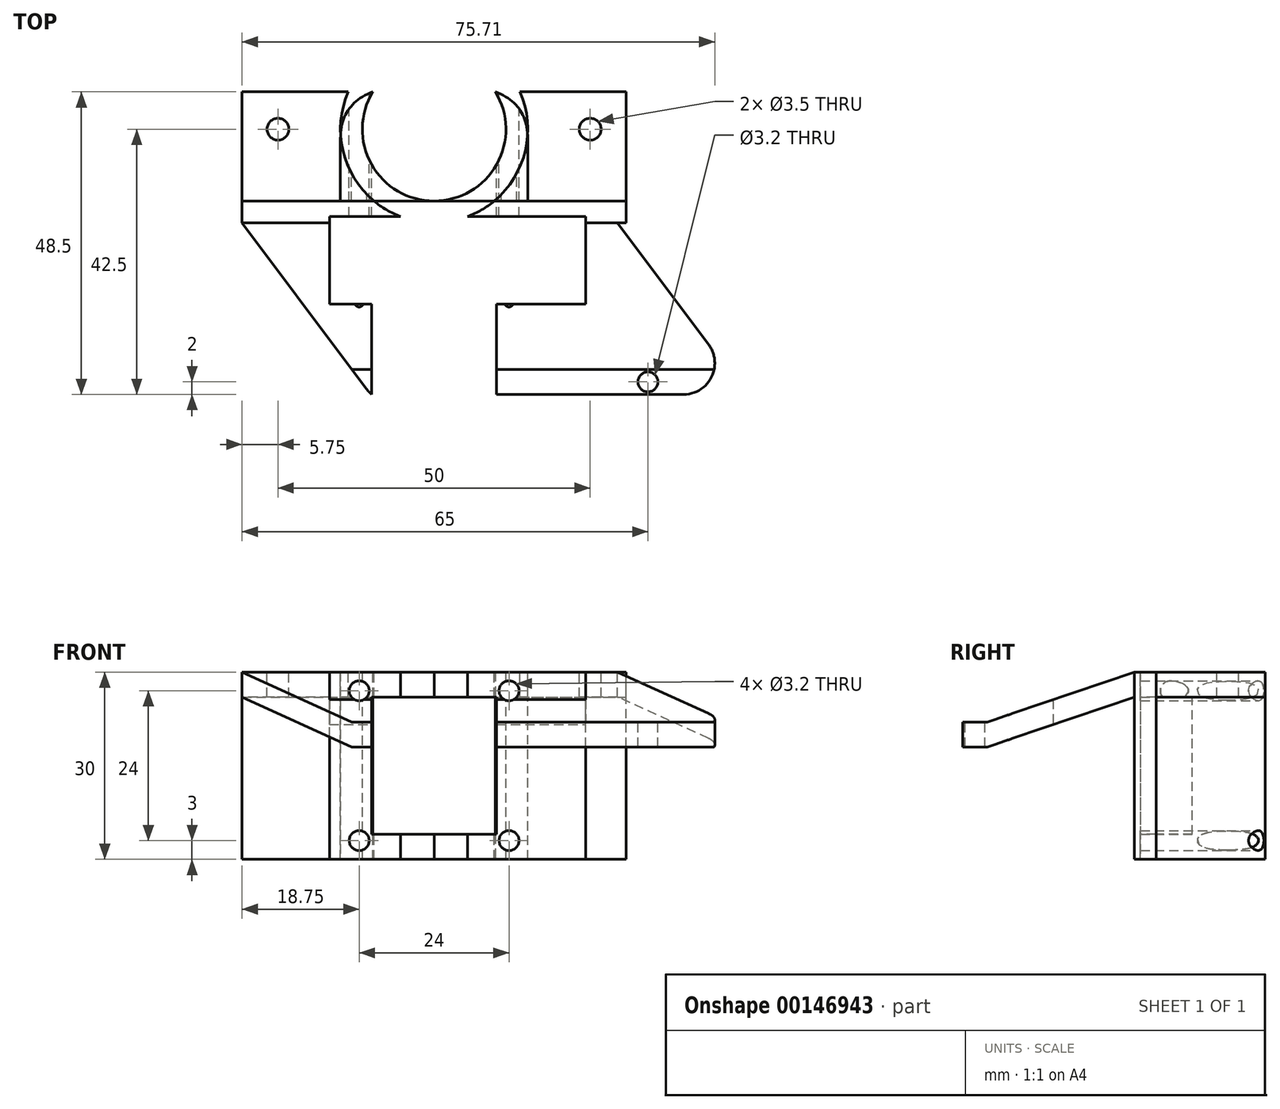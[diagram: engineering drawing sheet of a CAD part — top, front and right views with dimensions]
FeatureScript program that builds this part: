
annotation { "Feature Type Name" : "Feature", "Feature Type Description" : "" }
export const myFeature = defineFeature(function(context is Context, id is Id, definition is map)
    precondition{}
    {
        {
            var Q0;
            Q0=qCreatedBy(makeId("Top.planeOp"),FACE);
            var sketch = newSketch(context, id + "F0", { "sketchPlane" : qUnion([Q0])});
            skLineSegment(sketch, "E0", {"start": v(-25, 0) * mm, "end": v(25, 0) * mm, "construction": true});
            skCircle(sketch, "E1", {"center": v(0, 0) * mm, "radius": 15 * mm, "construction": true});
            skCircle(sketch, "E2", {"center": v(-25, 0) * mm, "radius": 1.75 * mm});
            skCircle(sketch, "E3", {"center": v(25, 0) * mm, "radius": 1.75 * mm});
            skLineSegment(sketch, "E4", {"start": v(-26.75, 0) * mm, "end": v(-30.75, 0) * mm, "construction": true});
            skLineSegment(sketch, "E5", {"start": v(26.75, 0) * mm, "end": v(30.75, 0) * mm, "construction": true});
            skLineSegment(sketch, "E6.bottom", {"start": v(-30.75, 6) * mm, "end": v(30.75, 6) * mm});
            skLineSegment(sketch, "E6.top", {"start": v(-30.75, -15) * mm, "end": v(30.75, -15) * mm});
            skLineSegment(sketch, "E6.left", {"start": v(-30.75, 6) * mm, "end": v(-30.75, -15) * mm});
            skLineSegment(sketch, "E6.right", {"start": v(30.75, 6) * mm, "end": v(30.75, -15) * mm});
            skArc(sketch, "E7", {"start": v(13.75, 6) * mm, "mid": v(0, -15) * mm, "end": v(-13.75, 6) * mm});
            skLineSegment(sketch, "E8.top", {"start": v(-30.75, -11.5) * mm, "end": v(30.75, -11.5) * mm});
            skLineSegment(sketch, "E8.left", {"start": v(-30.75, -15) * mm, "end": v(-30.75, -11.5) * mm});
            skLineSegment(sketch, "E8.right", {"start": v(30.75, -15) * mm, "end": v(30.75, -11.5) * mm});
            skCircle(sketch, "E9", {"center": v(0, 0) * mm, "radius": 11.5 * mm});
            skLineSegment(sketch, "E10", {"start": v(15, -11.5) * mm, "end": v(15, 0) * mm});
            skLineSegment(sketch, "E11", {"start": v(-15, 0) * mm, "end": v(-15, -11.5) * mm});
            skSolve(sketch);
        }
        {
            var Q0;
            Q0=makeQuery(id+"F0.imprint","IMPRINT",FACE,{"disambiguationData":[TD([[makeQuery(id+"F0.imprint","IMPRINT",EDGE,{"derivedFrom":sQuery(id+"F0.wireOp",EDGE,"E2")}),-1.0]])]});
            var Q1;
            {var subQ0=sQuery(id+"F0.wireOp",EDGE,"E11");Q1=makeQuery(id+"F0.imprint","IMPRINT",FACE,{"disambiguationData":[TD([[makeQuery(id+"F0.imprint","IMPRINT",EDGE,{"derivedFrom":subQ0}),1.0]])]});}
            var Q2;
            {var subQ0=sQuery(id+"F0.wireOp",EDGE,"E10");Q2=makeQuery(id+"F0.imprint","IMPRINT",FACE,{"disambiguationData":[TD([[makeQuery(id+"F0.imprint","IMPRINT",EDGE,{"derivedFrom":subQ0}),1.0]])]});}
            var Q3;
            Q3=makeQuery(id+"F0.imprint","IMPRINT",FACE,{"disambiguationData":[TD([[makeQuery(id+"F0.imprint","IMPRINT",EDGE,{"derivedFrom":sQuery(id+"F0.wireOp",EDGE,"E3")}),-1.0]])]});
            extrude(context, id + "F1", {"entities" : qUnion([Q0, Q1, Q2, Q3]), "oppositeDirection" : true, "depth" : 4 * mm, "offsetDistance" : 25 * mm});
        }
        {
            var Q0;
            Q0=makeQuery(id+"F0.imprint","IMPRINT",FACE,{"disambiguationData":[TD([[makeQuery(id+"F0.imprint","IMPRINT",EDGE,{"derivedFrom":sQuery(id+"F0.wireOp",EDGE,"E6.top")}),1.0]])]});
            var Q1;
            {var subQ0=sQuery(id+"F0.wireOp",EDGE,"E7");var subQ3=sQuery(id+"F0.wireOp",EDGE,"E6.bottom");var subQ4=makeQuery(id+"F0.imprint","INTERSECT",VERTEX,{"disambiguationData":[OD(1.0)],"derivedFrom":[subQ3,subQ0]});Q1=makeQuery(id+"F0.imprint","IMPRINT",FACE,{"disambiguationData":[TD([[makeQuery(id+"F0.imprint","IMPRINT",EDGE,{"disambiguationData":[TD([[subQ4,-1.0]])],"derivedFrom":subQ3}),-1.0]])]});}
            var Q2;
            {var subQ0=sQuery(id+"F0.wireOp",EDGE,"E11");Q2=makeQuery(id+"F0.imprint","IMPRINT",FACE,{"disambiguationData":[TD([[makeQuery(id+"F0.imprint","IMPRINT",EDGE,{"derivedFrom":subQ0}),1.0]])]});}
            var Q3;
            {var subQ0=sQuery(id+"F0.wireOp",EDGE,"E10");Q3=makeQuery(id+"F0.imprint","IMPRINT",FACE,{"disambiguationData":[TD([[makeQuery(id+"F0.imprint","IMPRINT",EDGE,{"derivedFrom":subQ0}),1.0]])]});}
            var Q4;
            {var subQ0=sQuery(id+"F0.wireOp",EDGE,"E7");var subQ4=sQuery(id+"F0.wireOp",EDGE,"E6.bottom");var subQ5=makeQuery(id+"F0.imprint","INTERSECT",VERTEX,{"disambiguationData":[OD(0.0)],"derivedFrom":[subQ4,subQ0]});Q4=makeQuery(id+"F0.imprint","IMPRINT",FACE,{"disambiguationData":[TD([[makeQuery(id+"F0.imprint","IMPRINT",EDGE,{"disambiguationData":[TD([[subQ5,1.0]])],"derivedFrom":subQ4}),-1.0]])]});}
            var Q5;
            {var subQ0=sQuery(id+"F0.wireOp",EDGE,"E7");var subQ1=makeQuery(id+"F0.imprint","INTERSECT",VERTEX,{"derivedFrom":[subQ0,sQuery(id+"F0.wireOp",EDGE,"E6.top")]});Q5=makeQuery(id+"F0.imprint","IMPRINT",FACE,{"disambiguationData":[TD([[makeQuery(id+"F0.imprint","IMPRINT",EDGE,{"disambiguationData":[TD([[subQ1,1.0]])],"derivedFrom":subQ0}),-1.0]])]});}
            extrude(context, id + "F2", {"entities" : qUnion([Q0, Q1, Q2, Q3, Q4, Q5]), "oppositeDirection" : true, "depth" : 30 * mm, "offsetDistance" : 25 * mm});
        }
        {
            var Q0;
            {var subQ0=sQuery(id+"F0.wireOp",EDGE,"E7");var subQ1=sQuery(id+"F0.wireOp",EDGE,"E6.bottom");Q0=makeQuery(id+"F2.opExtrude","SWEPT_EDGE",EDGE,{"disambiguationData":[OSD([subQ1,subQ0]),TDD([makeQuery(id+"F0.imprint","INTERSECT",VERTEX,{"disambiguationData":[OD(1.0)],"derivedFrom":[subQ1,subQ0]})])]});}
            var Q1;
            {var subQ0=sQuery(id+"F0.wireOp",EDGE,"E7");var subQ1=sQuery(id+"F0.wireOp",EDGE,"E6.bottom");Q1=makeQuery(id+"F2.opExtrude","SWEPT_EDGE",EDGE,{"disambiguationData":[OSD([subQ1,subQ0]),TDD([makeQuery(id+"F0.imprint","INTERSECT",VERTEX,{"disambiguationData":[OD(0.0)],"derivedFrom":[subQ1,subQ0]})])]});}
            fillet(context, id + "F3", {"entities" : qUnion([Q0, Q1]), "radius" : 8 * mm, "tangentPropagation" : true, "rho" : 0.5, "crossSection" : FilletCrossSection.CONIC, "allowEdgeOverflow" : false});
        }
        {
            var Q0;
            Q0=qCreatedBy(makeId("Front.planeOp"),FACE);
            var sketch = newSketch(context, id + "F4", { "sketchPlane" : qUnion([Q0])});
            skLineSegment(sketch, "E12", {"start": v(0, 0) * mm, "end": v(0, -30) * mm, "construction": true});
            skLineSegment(sketch, "E13.bottom", {"start": v(10, -4) * mm, "end": v(-10, -4) * mm});
            skLineSegment(sketch, "E13.top", {"start": v(10, -26) * mm, "end": v(-10, -26) * mm});
            skLineSegment(sketch, "E13.left", {"start": v(10, -4) * mm, "end": v(10, -26) * mm});
            skLineSegment(sketch, "E13.right", {"start": v(-10, -4) * mm, "end": v(-10, -26) * mm});
            skPoint(sketch, "E13.middle", {"position": v(0, -15) * mm});
            skLineSegment(sketch, "E14.bottom", {"start": v(12, -3) * mm, "end": v(-12, -3) * mm, "construction": true});
            skLineSegment(sketch, "E14.top", {"start": v(12, -27) * mm, "end": v(-12, -27) * mm, "construction": true});
            skLineSegment(sketch, "E14.left", {"start": v(12, -3) * mm, "end": v(12, -27) * mm, "construction": true});
            skLineSegment(sketch, "E14.right", {"start": v(-12, -3) * mm, "end": v(-12, -27) * mm, "construction": true});
            skCircle(sketch, "E15", {"center": v(12, -3) * mm, "radius": 1.6 * mm});
            skCircle(sketch, "E16", {"center": v(-12, -3) * mm, "radius": 1.6 * mm});
            skCircle(sketch, "E17", {"center": v(-12, -27) * mm, "radius": 1.6 * mm});
            skCircle(sketch, "E18", {"center": v(12, -27) * mm, "radius": 1.6 * mm});
            skSolve(sketch);
        }
        {
            var Q0;
            Q0=qCreatedBy(makeId("Right.planeOp"),FACE);
            var sketch = newSketch(context, id + "F5", { "sketchPlane" : qUnion([Q0])});
            skLineSegment(sketch, "E19", {"start": v(-40.5, 0) * mm, "end": v(0, 0) * mm, "construction": true});
            skLineSegment(sketch, "E20", {"start": v(-40.5, 0) * mm, "end": v(-40.5, -12) * mm, "construction": true});
            skLineSegment(sketch, "E21", {"start": v(-42.5, -12) * mm, "end": v(-38.5, -12) * mm});
            skLineSegment(sketch, "E22", {"start": v(-42.5, -12) * mm, "end": v(-42.5, -8) * mm});
            skLineSegment(sketch, "E23", {"start": v(-42.5, -8) * mm, "end": v(-38.5, -8) * mm});
            skLineSegment(sketch, "E24", {"start": v(-38.5, -8) * mm, "end": v(-38.5, -12) * mm});
            skLineSegment(sketch, "E25", {"start": v(-38.5, -8) * mm, "end": v(-15, 0) * mm});
            skLineSegment(sketch, "E26", {"start": v(-15, 0) * mm, "end": v(-15, -4) * mm});
            skLineSegment(sketch, "E27", {"start": v(-15, -4) * mm, "end": v(-15, 0) * mm});
            skLineSegment(sketch, "E28", {"start": v(-38.5, -12) * mm, "end": v(-15, -4) * mm});
            skSolve(sketch);
        }
        {
            var Q0;
            Q0=makeQuery(id+"F5.imprint","IMPRINT",FACE,{"disambiguationData":[TD([[makeQuery(id+"F5.imprint","IMPRINT",EDGE,{"derivedFrom":sQuery(id+"F5.wireOp",EDGE,"E21")}),1.0]])]});
            var Q1;
            Q1=makeQuery(id+"F5.imprint","IMPRINT",FACE,{"disambiguationData":[TD([[makeQuery(id+"F5.imprint","IMPRINT",EDGE,{"derivedFrom":sQuery(id+"F5.wireOp",EDGE,"E24")}),1.0]])]});
            extrude(context, id + "F6", {"entities" : qUnion([Q0, Q1]), "endBound" : BoundingType.SYMMETRIC, "depth" : 100 * mm});
        }
        {
            var Q0;
            Q0=makeQuery(id+"F4.imprint","IMPRINT",FACE,{"disambiguationData":[TD([[makeQuery(id+"F4.imprint","IMPRINT",EDGE,{"derivedFrom":sQuery(id+"F4.wireOp",EDGE,"E13.bottom")}),1.0]])]});
            extrude(context, id + "F7", {"entities" : qUnion([Q0]), "operationType" : NewBodyOperationType.REMOVE, "depth" : 111 * mm});
        }
        {
            var Q0;
            Q0=makeQuery(id+"F4.imprint","IMPRINT",FACE,{"disambiguationData":[TD([[makeQuery(id+"F4.imprint","IMPRINT",EDGE,{"derivedFrom":sQuery(id+"F4.wireOp",EDGE,"E15")}),1.0]])]});
            var Q1;
            Q1=makeQuery(id+"F4.imprint","IMPRINT",FACE,{"disambiguationData":[TD([[makeQuery(id+"F4.imprint","IMPRINT",EDGE,{"derivedFrom":sQuery(id+"F4.wireOp",EDGE,"E16")}),1.0]])]});
            var Q2;
            Q2=makeQuery(id+"F4.imprint","IMPRINT",FACE,{"disambiguationData":[TD([[makeQuery(id+"F4.imprint","IMPRINT",EDGE,{"derivedFrom":sQuery(id+"F4.wireOp",EDGE,"E17")}),1.0]])]});
            var Q3;
            Q3=makeQuery(id+"F4.imprint","IMPRINT",FACE,{"disambiguationData":[TD([[makeQuery(id+"F4.imprint","IMPRINT",EDGE,{"derivedFrom":sQuery(id+"F4.wireOp",EDGE,"E18")}),1.0]])]});
            extrude(context, id + "F8", {"entities" : qUnion([Q0, Q1, Q2, Q3]), "operationType" : NewBodyOperationType.REMOVE, "endBound" : BoundingType.SYMMETRIC, "depth" : 100 * mm});
        }
        {
            var Q0;
            Q0=qCreatedBy(makeId("Top.planeOp"),FACE);
            var sketch = newSketch(context, id + "F9", { "sketchPlane" : qUnion([Q0])});
            skLineSegment(sketch, "E29", {"start": v(-30.75, -40.5) * mm, "end": v(-5.75, -40.5) * mm, "construction": true});
            skLineSegment(sketch, "E30", {"start": v(-5.75, -40.5) * mm, "end": v(34.25, -40.5) * mm, "construction": true});
            skLineSegment(sketch, "E31", {"start": v(-30.75, -15) * mm, "end": v(-30.75, -38.5) * mm, "construction": true});
            skCircle(sketch, "E32", {"center": v(-5.75, -40.5) * mm, "radius": 1.6 * mm});
            skCircle(sketch, "E33", {"center": v(34.25, -40.5) * mm, "radius": 1.6 * mm});
            skLineSegment(sketch, "E34", {"start": v(-30.75, -15) * mm, "end": v(-10.16, -42.52) * mm});
            skLineSegment(sketch, "E35", {"start": v(49.96, -42.52) * mm, "end": v(29.37, -15) * mm});
            skLineSegment(sketch, "E36", {"start": v(29.37, -15) * mm, "end": v(-30.75, -15) * mm});
            skLineSegment(sketch, "E37", {"start": v(-30.75, -15) * mm, "end": v(-55.36, -15) * mm});
            skLineSegment(sketch, "E38", {"start": v(-55.36, -15) * mm, "end": v(-55.36, -47.4) * mm});
            skLineSegment(sketch, "E39", {"start": v(-55.36, -47.4) * mm, "end": v(60.75, -47.4) * mm});
            skLineSegment(sketch, "E40", {"start": v(60.75, -47.4) * mm, "end": v(60.75, -15) * mm});
            skLineSegment(sketch, "E41", {"start": v(60.75, -15) * mm, "end": v(29.37, -15) * mm});
            skLineSegment(sketch, "E42", {"start": v(49.96, -42.52) * mm, "end": v(-10.16, -42.52) * mm});
            skSolve(sketch);
        }
        {
            var Q0;
            Q0=makeQuery(id+"F9.imprint","IMPRINT",FACE,{"disambiguationData":[TD([[makeQuery(id+"F9.imprint","IMPRINT",EDGE,{"derivedFrom":sQuery(id+"F9.wireOp",EDGE,"E32")}),1.0]])]});
            var Q1;
            Q1=makeQuery(id+"F9.imprint","IMPRINT",FACE,{"disambiguationData":[TD([[makeQuery(id+"F9.imprint","IMPRINT",EDGE,{"derivedFrom":sQuery(id+"F9.wireOp",EDGE,"E33")}),1.0]])]});
            var Q2;
            Q2=makeQuery(id+"F9.imprint","IMPRINT",FACE,{"disambiguationData":[TD([[makeQuery(id+"F9.imprint","IMPRINT",EDGE,{"derivedFrom":sQuery(id+"F9.wireOp",EDGE,"E34")}),-1.0]])]});
            extrude(context, id + "F10", {"entities" : qUnion([Q0, Q1, Q2]), "operationType" : NewBodyOperationType.REMOVE, "oppositeDirection" : true, "depth" : 60 * mm});
        }
        {
            var Q0;
            Q0=makeQuery(id+"F10.boolean.opBoolean","COPY",EDGE,{"derivedFrom":makeQuery(id+"F10.opExtrude","SWEPT_EDGE",EDGE,{"disambiguationData":[OSD([sQuery(id+"F9.wireOp",EDGE,"E34"),sQuery(id+"F9.wireOp",EDGE,"LZ9jtE0i-OAHh-45kW-sWNW-y6qPTdp6gWfT")])]})});
            var Q1;
            Q1=makeQuery(id+"F10.boolean.opBoolean","COPY",EDGE,{"derivedFrom":makeQuery(id+"F10.opExtrude","SWEPT_EDGE",EDGE,{"disambiguationData":[OSD([sQuery(id+"F9.wireOp",EDGE,"LZ9jtE0i-OAHh-45kW-sWNW-y6qPTdp6gWfT"),sQuery(id+"F9.wireOp",EDGE,"E35")])]})});
            var Q2;
            Q2=makeQuery(id+"F10.boolean.opBoolean","INTERSECT",EDGE,{"derivedFrom":[makeQuery(id+"F6.opExtrude","SWEPT_FACE",FACE,{"disambiguationData":[OSD([sQuery(id+"F5.wireOp",EDGE,"E22")])]}),makeQuery(id+"F10.opExtrude","SWEPT_FACE",FACE,{"disambiguationData":[OSD([sQuery(id+"F9.wireOp",EDGE,"E34")])]})]});
            var Q3;
            Q3=makeQuery(id+"F10.boolean.opBoolean","INTERSECT",EDGE,{"derivedFrom":[makeQuery(id+"F6.opExtrude","SWEPT_FACE",FACE,{"disambiguationData":[OSD([sQuery(id+"F5.wireOp",EDGE,"E22")])]}),makeQuery(id+"F10.opExtrude","SWEPT_FACE",FACE,{"disambiguationData":[OSD([sQuery(id+"F9.wireOp",EDGE,"E35")])]})]});
            fillet(context, id + "F11", {"entities" : qUnion([Q0, Q1, Q2, Q3]), "radius" : 5 * mm, "tangentPropagation" : true, "allowEdgeOverflow" : false});
        }
        {
            var Q0;
            Q0=qCreatedBy(makeId("Front.planeOp"),FACE);
            var sketch = newSketch(context, id + "F12", { "sketchPlane" : qUnion([Q0])});
            skLineSegment(sketch, "E43", {"start": v(-16.75, 0) * mm, "end": v(-16.75, -31) * mm});
            skLineSegment(sketch, "E44", {"start": v(-16.75, 0) * mm, "end": v(24.25, 0) * mm});
            skLineSegment(sketch, "E45", {"start": v(24.25, 0) * mm, "end": v(24.25, -31) * mm});
            skLineSegment(sketch, "E46", {"start": v(24.25, -31) * mm, "end": v(-16.75, -31) * mm});
            skLineSegment(sketch, "E47", {"start": v(-16.75, -31) * mm, "end": v(24.25, -31) * mm});
            skSolve(sketch);
        }
        {
            var Q0;
            Q0=qSketchRegion(id+"F12",true);
            extrude(context, id + "F13", {"entities" : qUnion([Q0]), "operationType" : NewBodyOperationType.REMOVE, "depth" : 28 * mm, "hasSecondDirection" : true, "secondDirectionOppositeDirection" : false, "secondDirectionDepth" : 14 * mm});
        }
        {
            var Q0;
            Q0=makeQuery(id+"F6.opExtrude","SWEPT_FACE",FACE,{"disambiguationData":[OSD([sQuery(id+"F5.wireOp",EDGE,"E22")])]});
            var sketch = newSketch(context, id + "F14", { "sketchPlane" : qUnion([Q0])});
            skLineSegment(sketch, "E48", {"start": v(0, 20.47) * mm, "end": v(0, -59.46) * mm, "construction": true});
            skLineSegment(sketch, "E49", {"start": v(34.25, 1.98) * mm, "end": v(34.25, -22.25) * mm, "construction": true});
            skLineSegment(sketch, "E50", {"start": v(-5.75, 1.85) * mm, "end": v(-5.75, -20.16) * mm, "construction": true});
            skLineSegment(sketch, "E51", {"start": v(-7.67, -12) * mm, "end": v(-7.67, -15) * mm});
            skLineSegment(sketch, "E52", {"start": v(-7.67, -15) * mm, "end": v(39.96, -15) * mm});
            skLineSegment(sketch, "E53", {"start": v(39.96, -15) * mm, "end": v(39.96, -12) * mm});
            skLineSegment(sketch, "E54", {"start": v(39.96, -12) * mm, "end": v(-7.67, -12) * mm});
            skLineSegment(sketch, "E55.bottom", {"start": v(7.5, -15) * mm, "end": v(10.5, -15) * mm});
            skLineSegment(sketch, "E55.top", {"start": v(7.5, -35) * mm, "end": v(10.5, -35) * mm});
            skLineSegment(sketch, "E55.left", {"start": v(7.5, -15) * mm, "end": v(7.5, -35) * mm});
            skLineSegment(sketch, "E55.right", {"start": v(10.5, -15) * mm, "end": v(10.5, -35) * mm});
            skSolve(sketch);
        }
        {
            var Q0;
            Q0=makeQuery(id+"F14.imprint","IMPRINT",FACE,{"disambiguationData":[TD([[makeQuery(id+"F14.imprint","IMPRINT",EDGE,{"derivedFrom":sQuery(id+"F14.wireOp",EDGE,"E55.bottom")}),-1.0]])]});
            var Q1;
            {var subQ3=sQuery(id+"F14.wireOp",EDGE,"E51");Q1=makeQuery(id+"F14.imprint","IMPRINT",FACE,{"disambiguationData":[TD([[makeQuery(id+"F14.imprint","IMPRINT",EDGE,{"derivedFrom":subQ3}),1.0]])]});}
            extrude(context, id + "F15", {"entities" : qUnion([Q0, Q1]), "operationType" : NewBodyOperationType.ADD, "oppositeDirection" : true, "depth" : 5 * mm});
        }
        {
            var Q0;
            Q0=makeQuery(id+"F9.imprint","IMPRINT",FACE,{"disambiguationData":[TD([[makeQuery(id+"F9.imprint","IMPRINT",EDGE,{"derivedFrom":sQuery(id+"F9.wireOp",EDGE,"E33")}),1.0]])]});
            var Q1;
            Q1=makeQuery(id+"F9.imprint","IMPRINT",FACE,{"disambiguationData":[TD([[makeQuery(id+"F9.imprint","IMPRINT",EDGE,{"derivedFrom":sQuery(id+"F9.wireOp",EDGE,"E32")}),1.0]])]});
            extrude(context, id + "F16", {"entities" : qUnion([Q0, Q1]), "operationType" : NewBodyOperationType.REMOVE, "oppositeDirection" : true, "depth" : 25 * mm, "offsetDistance" : 25 * mm});
        }
        {
            var Q0;
            Q0=makeQuery(id+"F15.opExtrude","SWEPT_FACE",FACE,{"disambiguationData":[OSD([sQuery(id+"F14.wireOp",EDGE,"E55.right")])]});
            var sketch = newSketch(context, id + "F17", { "sketchPlane" : qUnion([Q0])});
            skLineSegment(sketch, "E56.bottom", {"start": v(-38.9, -17) * mm, "end": v(-41.1, -17) * mm});
            skLineSegment(sketch, "E56.top", {"start": v(-38.9, -33) * mm, "end": v(-41.1, -33) * mm});
            skLineSegment(sketch, "E56.left", {"start": v(-38.5, -17.4) * mm, "end": v(-38.5, -32.6) * mm});
            skLineSegment(sketch, "E56.right", {"start": v(-41.5, -17.4) * mm, "end": v(-41.5, -32.6) * mm});
            skPoint(sketch, "E56.middle", {"position": v(-40, -25) * mm});
            skPoint(sketch, "E57.visualSharp", {"position": v(-41.5, -17) * mm});
            skArc(sketch, "E57.filletArc", {"start": v(-41.1, -17) * mm, "mid": v(-41.38, -17.12) * mm, "end": v(-41.5, -17.4) * mm});
            skPoint(sketch, "E58.visualSharp", {"position": v(-38.5, -17) * mm});
            skArc(sketch, "E58.filletArc", {"start": v(-38.5, -17.4) * mm, "mid": v(-38.62, -17.12) * mm, "end": v(-38.9, -17) * mm});
            skPoint(sketch, "E59.visualSharp", {"position": v(-38.5, -33) * mm});
            skArc(sketch, "E59.filletArc", {"start": v(-38.9, -33) * mm, "mid": v(-38.62, -32.88) * mm, "end": v(-38.5, -32.6) * mm});
            skPoint(sketch, "E60.visualSharp", {"position": v(-41.5, -33) * mm});
            skArc(sketch, "E60.filletArc", {"start": v(-41.5, -32.6) * mm, "mid": v(-41.38, -32.88) * mm, "end": v(-41.1, -33) * mm});
            skLineSegment(sketch, "E61", {"start": v(-40, -12) * mm, "end": v(-40, -46) * mm, "construction": true});
            skPoint(sketch, "E61.startSnap0", {"position": v(-40, -15) * mm});
            skPoint(sketch, "E61.endSnap0", {"position": v(-40, -35) * mm});
            skSolve(sketch);
        }
        {
            var Q0;
            Q0=makeQuery(id+"F17.imprint","IMPRINT",FACE,{"disambiguationData":[TD([[makeQuery(id+"F17.imprint","IMPRINT",EDGE,{"derivedFrom":sQuery(id+"F17.wireOp",EDGE,"E56.bottom")}),1.0]])]});
            var Q1;
            Q1 = qSketchRegion(id + "F14", true);
            extrude(context, id + "F18", {"entities" : qUnion([Q0, Q1]), "operationType" : NewBodyOperationType.REMOVE, "oppositeDirection" : true, "depth" : 25 * mm, "offsetDistance" : 25 * mm});
        }
    });
